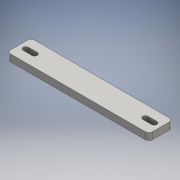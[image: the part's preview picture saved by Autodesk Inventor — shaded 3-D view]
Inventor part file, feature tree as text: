
AUTODESK INVENTOR PART (.ipt)
format: ipt  version: 2016 (Build 200138000, 138)  size: 113,152 bytes
history: native  units: mm
features: extrude x1, fillet x1, sketch x1
ambient origin geometry x8: Origin, YZ Plane, XZ Plane, XY Plane, X Axis, Y Axis, Z Axis, Center Point
bodies: Solid1 (feature_tree)
feature tree (3):
  extrude  "Extrusion1"  Depth=8.0mm TaperAngle=0.0deg
  fillet  "Fillet1"  Radius=4.0mm
  sketch  "Sketch1"  dims[d0=160.0mm d1=27.0mm d2=10.0mm d3=10.0mm d4=8.0mm d5=0.0mm d6=4.0mm d7=6.0mm d8=10.5mm d9=6.0mm d10=10.5mm]
